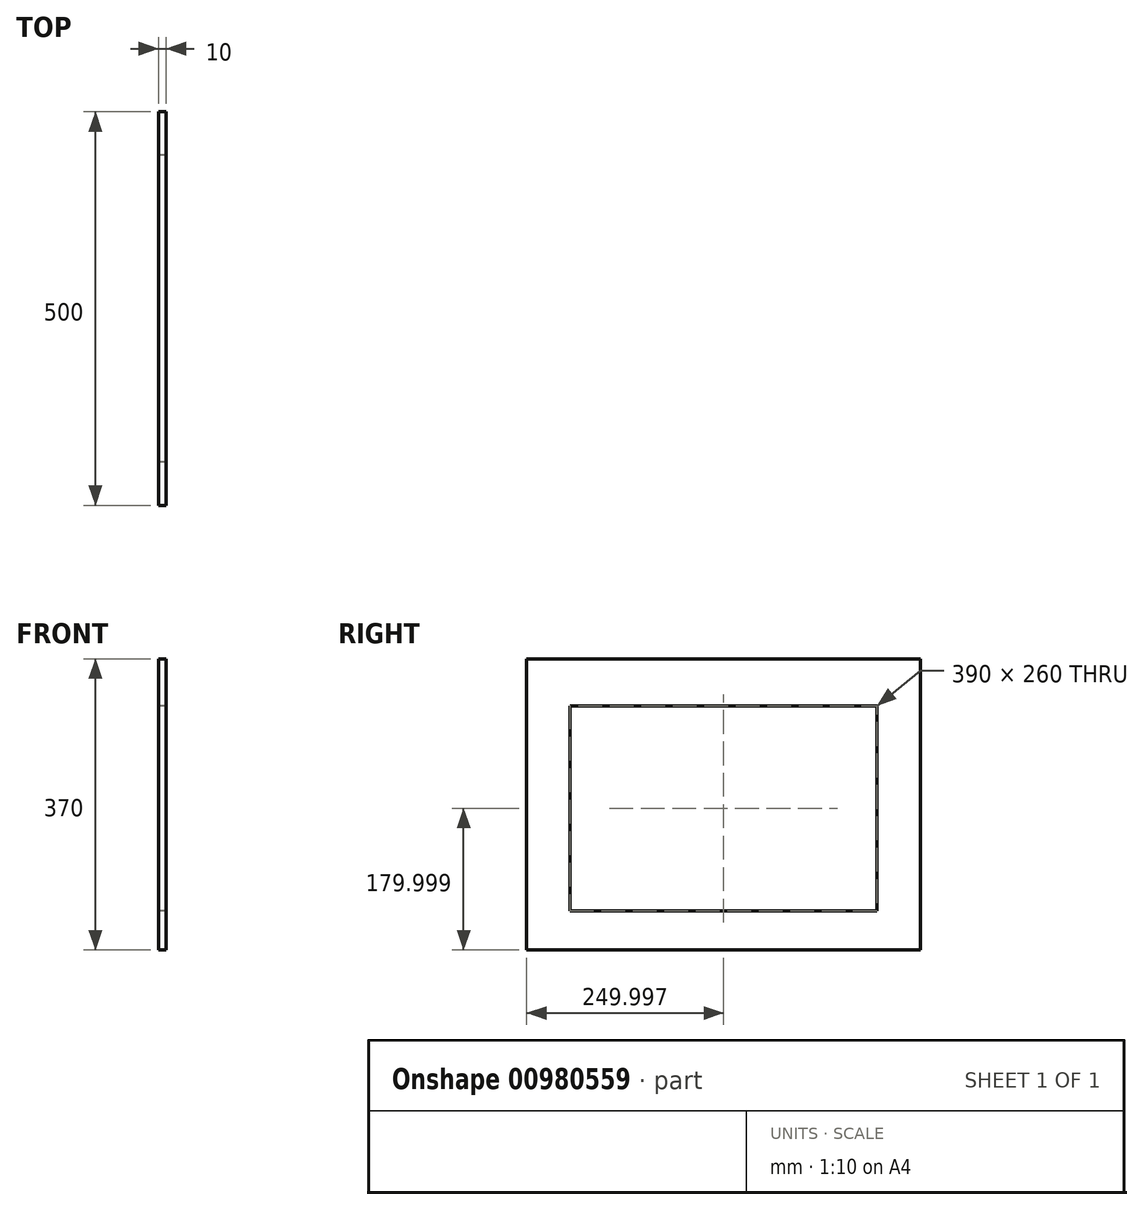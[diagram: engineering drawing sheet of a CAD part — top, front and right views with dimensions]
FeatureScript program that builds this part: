
annotation { "Feature Type Name" : "Feature", "Feature Type Description" : "" }
export const myFeature = defineFeature(function(context is Context, id is Id, definition is map)
    precondition{}
    {
        {
            var Q0;
            Q0=qCreatedBy(makeId("Right.planeOp"),FACE);
            var sketch = newSketch(context, id + "F0", { "sketchPlane" : qUnion([Q0])});
            skLineSegment(sketch, "E0.bottom", {"start": v(-179.76, 102.6) * mm, "end": v(210.24, 102.6) * mm});
            skLineSegment(sketch, "E0.top", {"start": v(-179.76, -157.4) * mm, "end": v(210.24, -157.4) * mm});
            skLineSegment(sketch, "E0.left", {"start": v(-179.76, 102.6) * mm, "end": v(-179.76, -157.4) * mm});
            skLineSegment(sketch, "E0.right", {"start": v(210.24, 102.6) * mm, "end": v(210.24, -157.4) * mm});
            skLineSegment(sketch, "E1.bottom", {"start": v(-234.76, 162.6) * mm, "end": v(265.24, 162.6) * mm});
            skLineSegment(sketch, "E1.top", {"start": v(-234.76, -207.4) * mm, "end": v(265.24, -207.4) * mm});
            skLineSegment(sketch, "E1.left", {"start": v(-234.76, 162.6) * mm, "end": v(-234.76, -207.4) * mm});
            skLineSegment(sketch, "E1.right", {"start": v(265.24, 162.6) * mm, "end": v(265.24, -207.4) * mm});
            skSolve(sketch);
        }
        {
            var Q0;
            Q0 = qSketchRegion(id + "F0", true);
            extrude(context, id + "F1", {"entities" : qUnion([Q0]), "depth" : 10 * mm, "offsetDistance" : 25.4 * mm});
        }
    });
